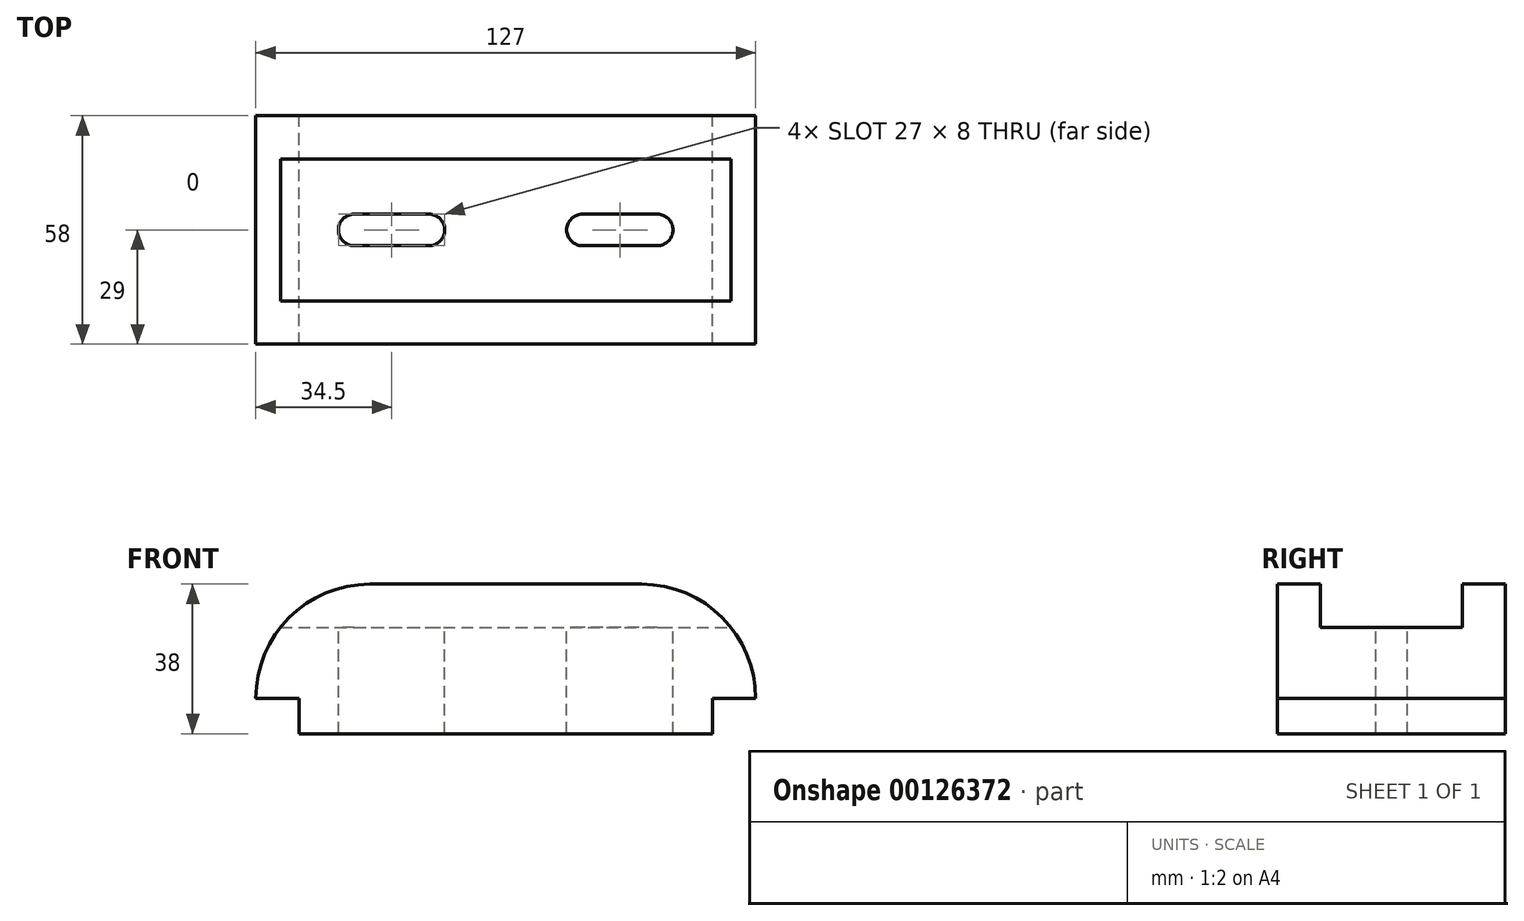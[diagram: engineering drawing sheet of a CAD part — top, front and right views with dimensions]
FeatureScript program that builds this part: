
annotation { "Feature Type Name" : "Feature", "Feature Type Description" : "" }
export const myFeature = defineFeature(function(context is Context, id is Id, definition is map)
    precondition{}
    {
        {
            var Q0;
            Q0=qCreatedBy(makeId("Front.planeOp"),FACE);
            var sketch = newSketch(context, id + "F0", { "sketchPlane" : qUnion([Q0])});
            skLineSegment(sketch, "E0", {"start": v(0, 0) * mm, "end": v(0, 66.4) * mm, "construction": true});
            skLineSegment(sketch, "E1", {"start": v(0, 0) * mm, "end": v(-52.5, 0) * mm});
            skLineSegment(sketch, "E2", {"start": v(-52.5, 0) * mm, "end": v(-52.5, 9) * mm});
            skLineSegment(sketch, "E3", {"start": v(-52.5, 9) * mm, "end": v(-63.5, 9) * mm});
            skArc(sketch, "E4", {"start": v(-34.5, 38) * mm, "mid": v(-55, 29.5) * mm, "end": v(-63.5, 9) * mm});
            skLineSegment(sketch, "E5", {"start": v(-34.5, 38) * mm, "end": v(0, 38) * mm});
            skLineSegment(sketch, "E6.MirrorCS", {"start": v(0, 0) * mm, "end": v(52.5, 0) * mm});
            skLineSegment(sketch, "E7.MirrorCS", {"start": v(52.5, 0) * mm, "end": v(52.5, 9) * mm});
            skLineSegment(sketch, "E8.MirrorCS", {"start": v(34.5, 38) * mm, "end": v(0, 38) * mm});
            skArc(sketch, "E9.MirrorCS", {"start": v(34.5, 38) * mm, "mid": v(55, 29.5) * mm, "end": v(63.5, 9) * mm});
            skLineSegment(sketch, "E10.MirrorCS", {"start": v(52.5, 9) * mm, "end": v(63.5, 9) * mm});
            skSolve(sketch);
        }
        {
            var Q0;
            Q0 = qSketchRegion(id + "F0", true);
            extrude(context, id + "F1", {"entities" : qUnion([Q0]), "depth" : 58 * mm});
        }
        {
            var Q0;
            Q0=makeQuery(id+"F1.opExtrude","SWEPT_FACE",FACE,{"disambiguationData":[OSD([sQuery(id+"F0.wireOp",EDGE,"E5"),sQuery(id+"F0.wireOp",EDGE,"E8.MirrorCS")])]});
            var sketch = newSketch(context, id + "F2", { "sketchPlane" : qUnion([Q0])});
            skLineSegment(sketch, "E11.bottom", {"start": v(-63.5, -11) * mm, "end": v(63.5, -11) * mm});
            skLineSegment(sketch, "E11.top", {"start": v(-63.5, -47) * mm, "end": v(63.5, -47) * mm});
            skLineSegment(sketch, "E11.left", {"start": v(-63.5, -11) * mm, "end": v(-63.5, -47) * mm});
            skLineSegment(sketch, "E11.right", {"start": v(63.5, -11) * mm, "end": v(63.5, -47) * mm});
            skSolve(sketch);
        }
        {
            var Q0;
            Q0 = qSketchRegion(id + "F2", true);
            extrude(context, id + "F3", {"entities" : qUnion([Q0]), "operationType" : NewBodyOperationType.REMOVE, "oppositeDirection" : true, "depth" : 11 * mm});
        }
        {
            var Q0;
            Q0=makeQuery(id+"F3.boolean.opBoolean","COPY",FACE,{"derivedFrom":makeQuery(id+"F3.opExtrude","CAP_FACE",FACE,{"disambiguationData":[OSD([sQuery(id+"F2.wireOp",EDGE,"E11.bottom"),sQuery(id+"F2.wireOp",EDGE,"E11.top"),sQuery(id+"F2.wireOp",EDGE,"E11.left"),sQuery(id+"F2.wireOp",EDGE,"E11.right")])],"isStart":false})});
            var sketch = newSketch(context, id + "F4", { "sketchPlane" : qUnion([Q0])});
            skLineSegment(sketch, "E12", {"start": v(0, 0) * mm, "end": v(0, -53.99) * mm, "construction": true});
            skArc(sketch, "E13", {"start": v(-38.5, -25) * mm, "mid": v(-42.5, -29) * mm, "end": v(-38.5, -33) * mm});
            skArc(sketch, "E14", {"start": v(-19.5, -33) * mm, "mid": v(-15.5, -29) * mm, "end": v(-19.5, -25) * mm});
            skLineSegment(sketch, "E15", {"start": v(-38.5, -25) * mm, "end": v(-19.5, -25) * mm});
            skLineSegment(sketch, "E16", {"start": v(-38.5, -33) * mm, "end": v(-19.5, -33) * mm});
            skLineSegment(sketch, "E17.MirrorCS", {"start": v(38.5, -25) * mm, "end": v(19.5, -25) * mm});
            skLineSegment(sketch, "E18.MirrorCS", {"start": v(38.5, -33) * mm, "end": v(19.5, -33) * mm});
            skArc(sketch, "E19.MirrorCS", {"start": v(19.5, -33) * mm, "mid": v(15.5, -29) * mm, "end": v(19.5, -25) * mm});
            skArc(sketch, "E20.MirrorCS", {"start": v(38.5, -25) * mm, "mid": v(42.5, -29) * mm, "end": v(38.5, -33) * mm});
            skSolve(sketch);
        }
        {
            var Q0;
            Q0 = qSketchRegion(id + "F4", true);
            extrude(context, id + "F5", {"entities" : qUnion([Q0]), "operationType" : NewBodyOperationType.REMOVE, "endBound" : BoundingType.THROUGH_ALL, "oppositeDirection" : true, "depth" : 25 * mm});
        }
    });
